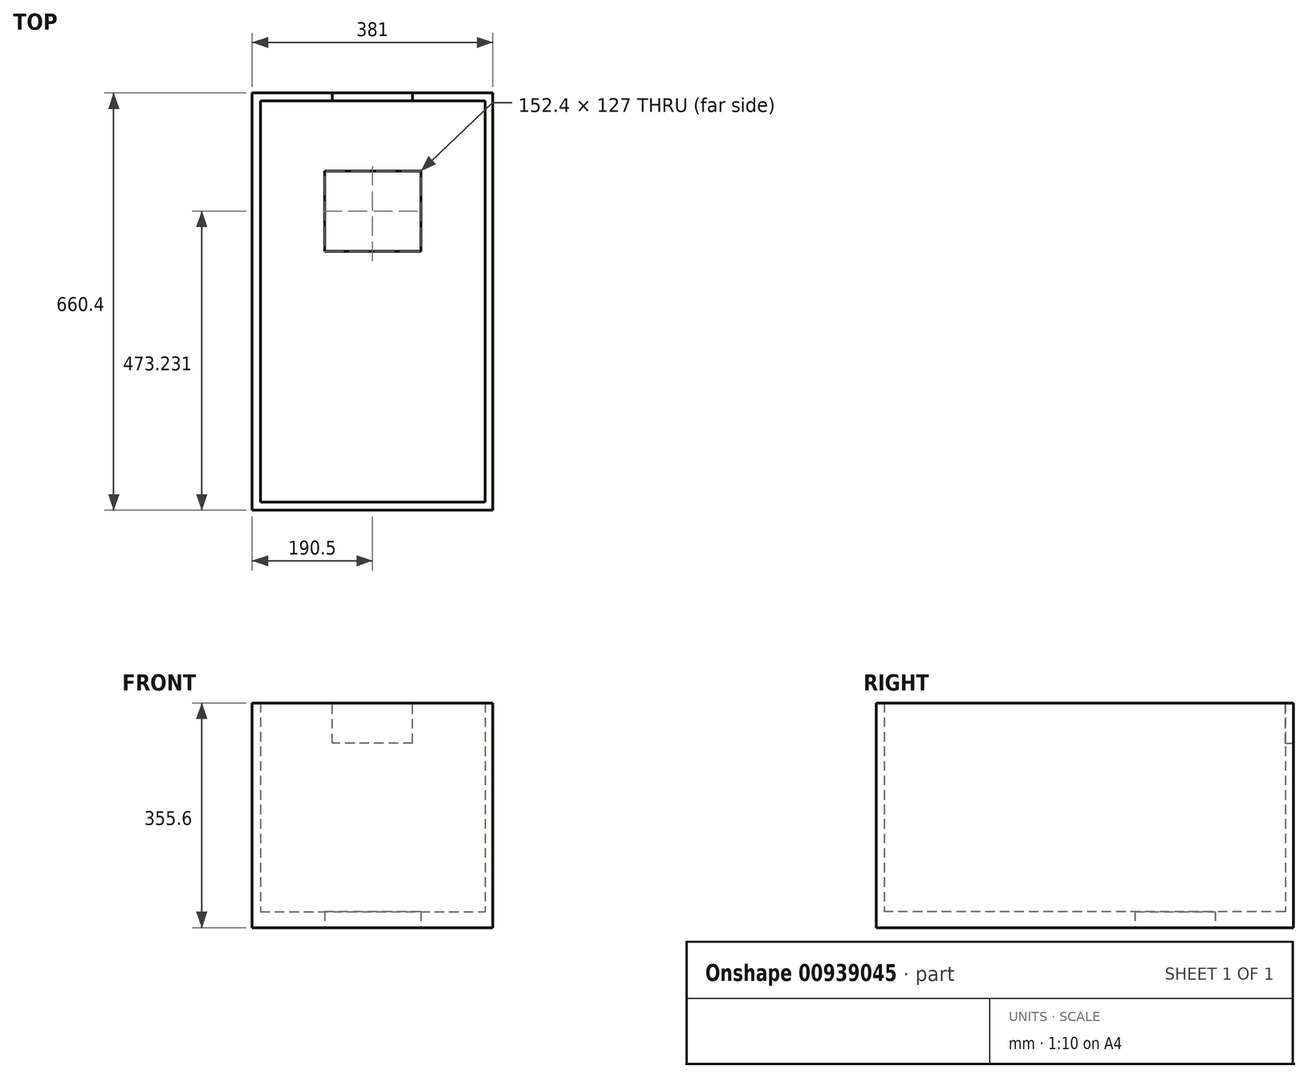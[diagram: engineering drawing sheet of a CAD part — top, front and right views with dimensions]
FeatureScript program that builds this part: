
annotation { "Feature Type Name" : "Feature", "Feature Type Description" : "" }
export const myFeature = defineFeature(function(context is Context, id is Id, definition is map)
    precondition{}
    {
        {
            var Q0;
            Q0=qCreatedBy(makeId("Top.planeOp"),FACE);
            var sketch = newSketch(context, id + "F0", { "sketchPlane" : qUnion([Q0])});
            skLineSegment(sketch, "E0.bottom", {"start": v(190.5, 330.2) * mm, "end": v(-190.5, 330.2) * mm});
            skLineSegment(sketch, "E0.top", {"start": v(190.5, -330.2) * mm, "end": v(-190.5, -330.2) * mm});
            skLineSegment(sketch, "E0.left", {"start": v(190.5, 330.2) * mm, "end": v(190.5, -330.2) * mm});
            skLineSegment(sketch, "E0.right", {"start": v(-190.5, 330.2) * mm, "end": v(-190.5, -330.2) * mm});
            skPoint(sketch, "E0.middle", {"position": v(0, 0) * mm});
            skLineSegment(sketch, "E1.bottom", {"start": v(-177.8, 317.5) * mm, "end": v(177.8, 317.5) * mm});
            skLineSegment(sketch, "E1.top", {"start": v(-177.8, -317.5) * mm, "end": v(177.8, -317.5) * mm});
            skLineSegment(sketch, "E1.left", {"start": v(-177.8, 317.5) * mm, "end": v(-177.8, -317.5) * mm});
            skLineSegment(sketch, "E1.right", {"start": v(177.8, 317.5) * mm, "end": v(177.8, -317.5) * mm});
            skSolve(sketch);
        }
        {
            var Q0;
            Q0 = qSketchRegion(id + "F0", true);
            extrude(context, id + "F1", {"entities" : qUnion([Q0]), "depth" : 355.6 * mm, "offsetDistance" : 25.4 * mm});
        }
        {
            var Q0;
            Q0=makeQuery(id+"F0.imprint","IMPRINT",FACE,{"disambiguationData":[TD([[makeQuery(id+"F0.imprint","IMPRINT",EDGE,{"derivedFrom":sQuery(id+"F0.wireOp",EDGE,"E1.bottom")}),-1.0]])]});
            extrude(context, id + "F2", {"entities" : qUnion([Q0]), "operationType" : NewBodyOperationType.ADD, "depth" : 25.4 * mm, "offsetDistance" : 25.4 * mm});
        }
        {
            var Q0;
            Q0=makeQuery(id+"F0.imprint","IMPRINT",FACE,{"disambiguationData":[TD([[makeQuery(id+"F0.imprint","IMPRINT",EDGE,{"derivedFrom":sQuery(id+"F0.wireOp",EDGE,"E1.bottom")}),-1.0]])]});
            var sketch = newSketch(context, id + "F3", { "sketchPlane" : qUnion([Q0])});
            skLineSegment(sketch, "E2", {"start": v(0, 276.07) * mm, "end": v(0, 79.53) * mm});
            skLineSegment(sketch, "E3.bottom", {"start": v(0, 79.53) * mm, "end": v(-76.2, 79.53) * mm});
            skLineSegment(sketch, "E3.top", {"start": v(0, 206.53) * mm, "end": v(-76.2, 206.53) * mm});
            skLineSegment(sketch, "E3.left", {"start": v(0, 79.53) * mm, "end": v(0, 206.53) * mm});
            skLineSegment(sketch, "E3.right", {"start": v(-76.2, 79.53) * mm, "end": v(-76.2, 206.53) * mm});
            skLineSegment(sketch, "E4.bottom", {"start": v(0, 79.53) * mm, "end": v(76.2, 79.53) * mm});
            skLineSegment(sketch, "E4.top", {"start": v(0, 206.53) * mm, "end": v(76.2, 206.53) * mm});
            skLineSegment(sketch, "E4.right", {"start": v(76.2, 79.53) * mm, "end": v(76.2, 206.53) * mm});
            skSolve(sketch);
        }
        {
            var Q0;
            {var subQ3=sQuery(id+"F3.wireOp",EDGE,"E4.bottom");var subQ4=sQuery(id+"F3.wireOp",EDGE,"E3.bottom");Q0=qUnion([makeQuery(id+"F3.imprint","IMPRINT",FACE,{"disambiguationData":[TD([[makeQuery(id+"F3.imprint","IMPRINT",EDGE,{"derivedFrom":subQ4}),-1.0]])]}),makeQuery(id+"F3.imprint","IMPRINT",FACE,{"disambiguationData":[TD([[makeQuery(id+"F3.imprint","IMPRINT",EDGE,{"derivedFrom":subQ3}),1.0]])]})]);}
            extrude(context, id + "F4", {"entities" : qUnion([Q0]), "operationType" : NewBodyOperationType.REMOVE, "depth" : 25.4 * mm, "offsetDistance" : 25.4 * mm});
        }
        {
            var Q0;
            Q0=makeQuery(id+"F1.opExtrude","SWEPT_FACE",FACE,{"disambiguationData":[OSD([sQuery(id+"F0.wireOp",EDGE,"E0.bottom")])]});
            var sketch = newSketch(context, id + "F5", { "sketchPlane" : qUnion([Q0])});
            skLineSegment(sketch, "E5.bottom", {"start": v(-63.5, 292.1) * mm, "end": v(63.5, 292.1) * mm});
            skLineSegment(sketch, "E5.top", {"start": v(-63.5, 419.1) * mm, "end": v(63.5, 419.1) * mm});
            skLineSegment(sketch, "E5.left", {"start": v(-63.5, 292.1) * mm, "end": v(-63.5, 419.1) * mm});
            skLineSegment(sketch, "E5.right", {"start": v(63.5, 292.1) * mm, "end": v(63.5, 419.1) * mm});
            skPoint(sketch, "E5.middle", {"position": v(0, 355.6) * mm});
            skSolve(sketch);
        }
        {
            var Q0;
            Q0 = qSketchRegion(id + "F5", true);
            extrude(context, id + "F6", {"entities" : qUnion([Q0]), "operationType" : NewBodyOperationType.REMOVE, "oppositeDirection" : true, "depth" : 25.4 * mm, "offsetDistance" : 25.4 * mm});
        }
    });
